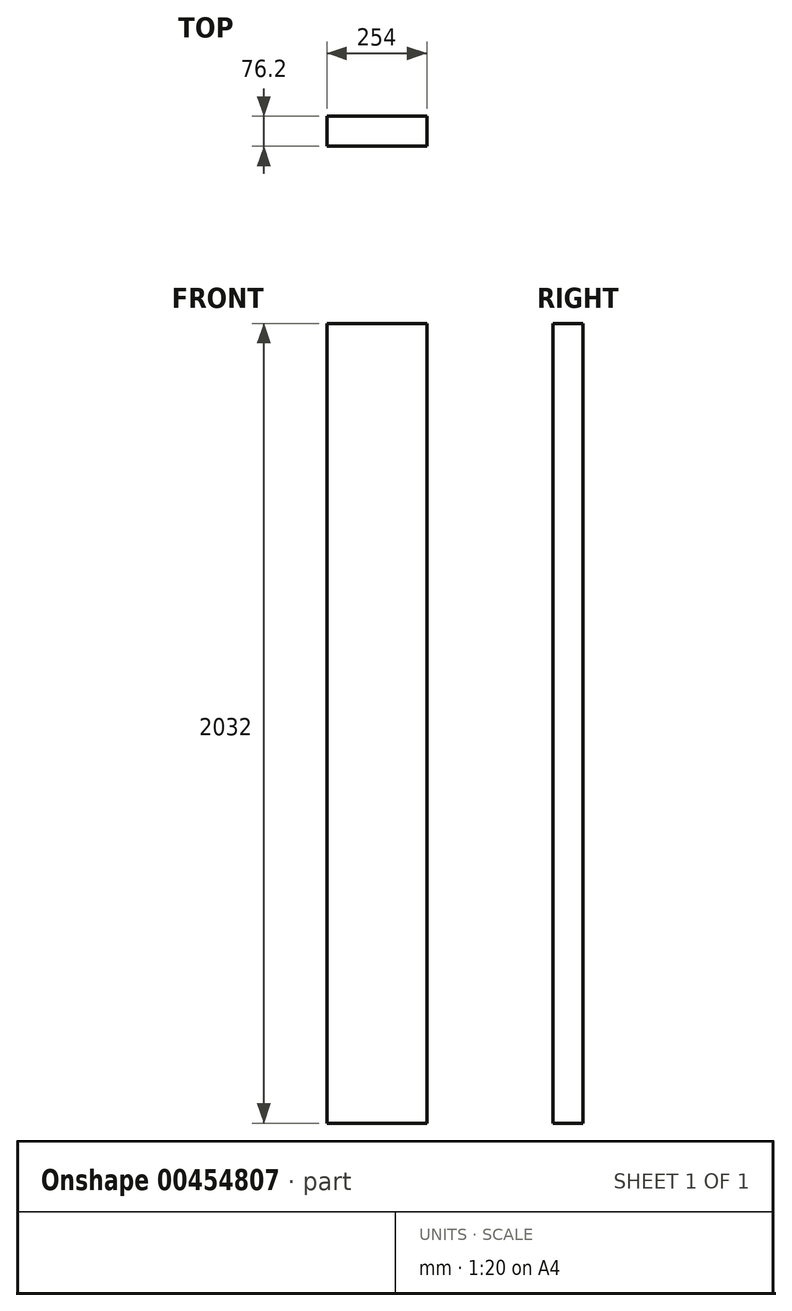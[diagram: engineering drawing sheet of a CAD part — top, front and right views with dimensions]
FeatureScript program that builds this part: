
annotation { "Feature Type Name" : "Feature", "Feature Type Description" : "" }
export const myFeature = defineFeature(function(context is Context, id is Id, definition is map)
    precondition{}
    {
        {
            var Q0;
            Q0=qCreatedBy(makeId("Top.planeOp"),FACE);
            var sketch = newSketch(context, id + "F0", { "sketchPlane" : qUnion([Q0])});
            skLineSegment(sketch, "E0.bottom", {"start": v(-127.82, 25.4) * mm, "end": v(126.18, 25.4) * mm});
            skLineSegment(sketch, "E0.top", {"start": v(-127.82, -50.8) * mm, "end": v(126.18, -50.8) * mm});
            skLineSegment(sketch, "E0.left", {"start": v(-127.82, 25.4) * mm, "end": v(-127.82, -50.8) * mm});
            skLineSegment(sketch, "E0.right", {"start": v(126.18, 25.4) * mm, "end": v(126.18, -50.8) * mm});
            skSolve(sketch);
        }
        {
            var Q0;
            Q0=makeQuery(id+"F0.imprint","IMPRINT",FACE,{"disambiguationData":[TD([[makeQuery(id+"F0.imprint","IMPRINT",EDGE,{"derivedFrom":sQuery(id+"F0.wireOp",EDGE,"E0.bottom")}),-1.0]])]});
            extrude(context, id + "F1", {"entities" : qUnion([Q0]), "endBound" : BoundingType.SYMMETRIC, "depth" : 2032 * mm});
        }
    });
